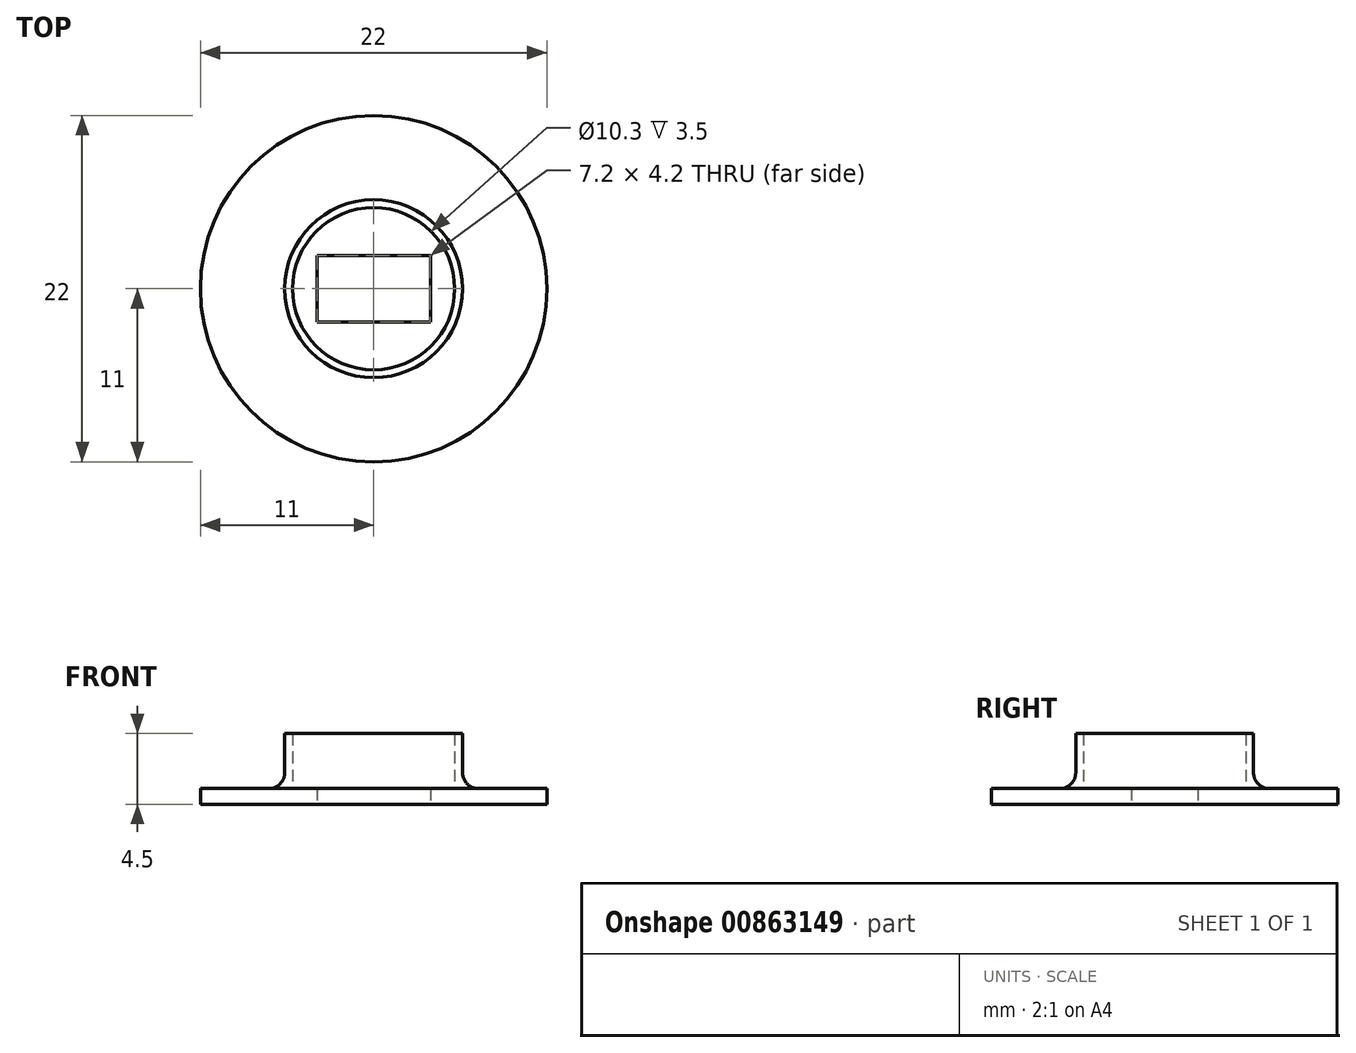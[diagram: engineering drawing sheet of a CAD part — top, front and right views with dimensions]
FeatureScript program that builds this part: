
annotation { "Feature Type Name" : "Feature", "Feature Type Description" : "" }
export const myFeature = defineFeature(function(context is Context, id is Id, definition is map)
    precondition{}
    {
        {
            var Q0;
            Q0=qCreatedBy(makeId("Top.planeOp"),FACE);
            var sketch = newSketch(context, id + "F0", { "sketchPlane" : qUnion([Q0])});
            skCircle(sketch, "E0", {"center": v(0, 0) * mm, "radius": 5.65 * mm});
            skCircle(sketch, "E1", {"center": v(0, 0) * mm, "radius": 5.15 * mm});
            skSolve(sketch);
        }
        {
            var Q0;
            Q0=qCreatedBy(makeId("Top.planeOp"),FACE);
            var sketch = newSketch(context, id + "F1", { "sketchPlane" : qUnion([Q0])});
            skCircle(sketch, "E2", {"center": v(0, 0) * mm, "radius": 11 * mm});
            skLineSegment(sketch, "E3.bottom", {"start": v(-3.6, 2.1) * mm, "end": v(3.6, 2.1) * mm});
            skLineSegment(sketch, "E3.top", {"start": v(-3.6, -2.1) * mm, "end": v(3.6, -2.1) * mm});
            skLineSegment(sketch, "E3.left", {"start": v(-3.6, 2.1) * mm, "end": v(-3.6, -2.1) * mm});
            skLineSegment(sketch, "E3.right", {"start": v(3.6, 2.1) * mm, "end": v(3.6, -2.1) * mm});
            skSolve(sketch);
        }
        {
            var Q0;
            Q0=qSketchRegion(id+"F1",true);
            extrude(context, id + "F2", {"entities" : qUnion([Q0]), "depth" : 1 * mm, "offsetDistance" : 25 * mm});
        }
        {
            var Q0;
            Q0=qSketchRegion(id+"F0",true);
            extrude(context, id + "F3", {"entities" : qUnion([Q0]), "operationType" : NewBodyOperationType.ADD, "depth" : 4.5 * mm, "offsetDistance" : 25 * mm});
        }
        {
            var Q0;
            Q0=makeQuery(id+"F3.boolean.opBoolean","INTERSECT",EDGE,{"derivedFrom":[makeQuery(id+"F2.opExtrude","CAP_FACE",FACE,{"disambiguationData":[OSD([sQuery(id+"F1.wireOp",EDGE,"E2"),sQuery(id+"F1.wireOp",EDGE,"E3.bottom"),sQuery(id+"F1.wireOp",EDGE,"E3.top"),sQuery(id+"F1.wireOp",EDGE,"E3.left"),sQuery(id+"F1.wireOp",EDGE,"E3.right")])],"isStart":false}),makeQuery(id+"F3.opExtrude","SWEPT_FACE",FACE,{"disambiguationData":[OSD([sQuery(id+"F0.wireOp",EDGE,"E0")])]})]});
            fillet(context, id + "F4", {"entities" : qUnion([Q0]), "radius" : 1 * mm, "tangentPropagation" : true, "allowEdgeOverflow" : false});
        }
    });
